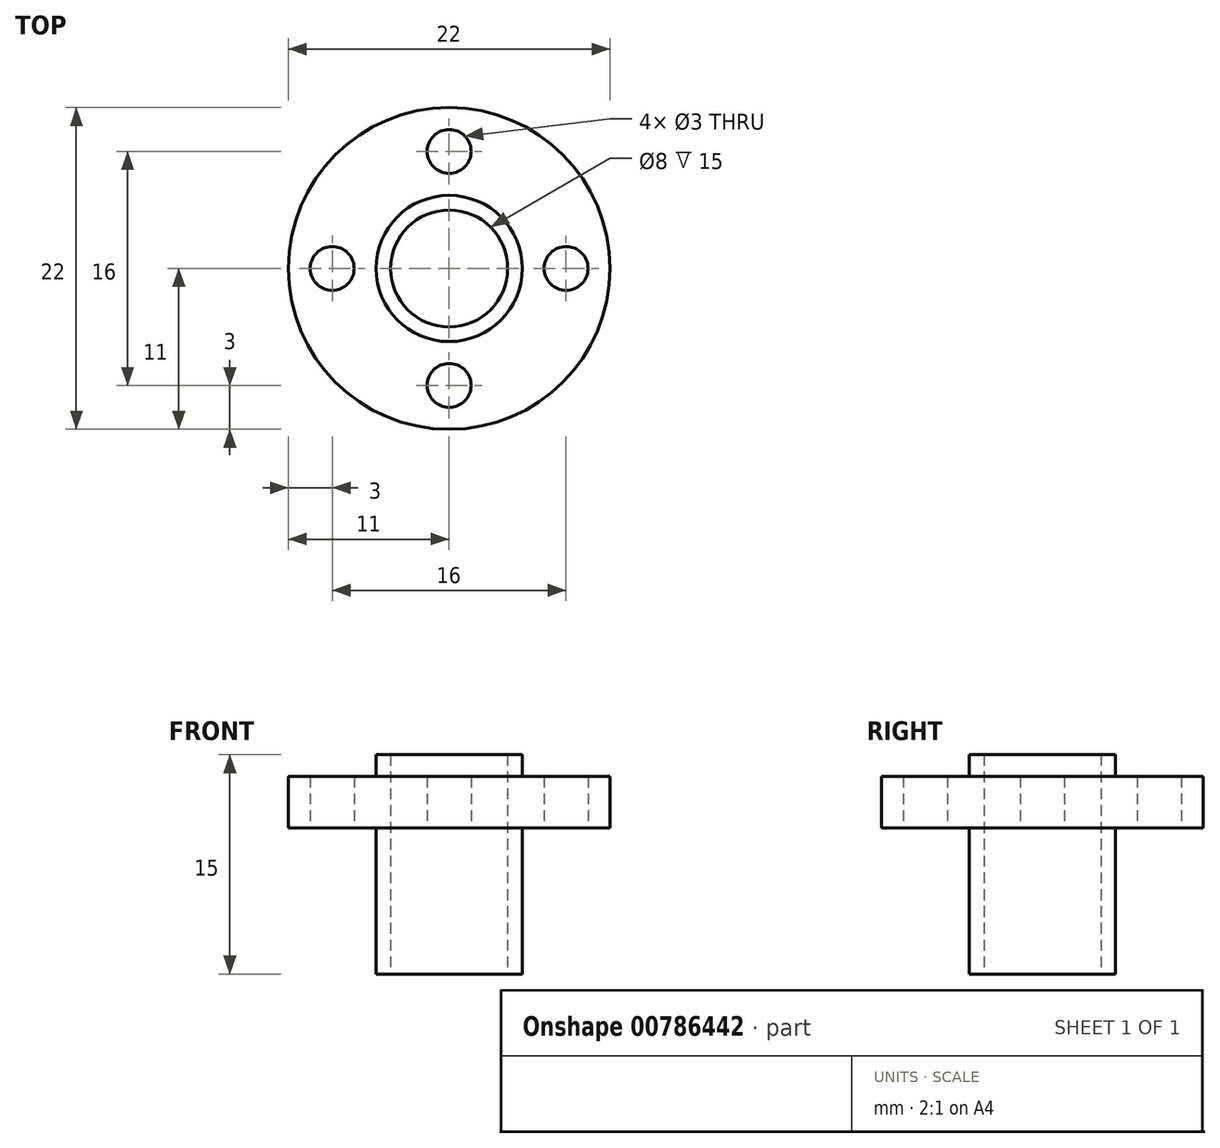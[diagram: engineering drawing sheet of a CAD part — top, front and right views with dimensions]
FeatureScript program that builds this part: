
annotation { "Feature Type Name" : "Feature", "Feature Type Description" : "" }
export const myFeature = defineFeature(function(context is Context, id is Id, definition is map)
    precondition{}
    {
        {
            var Q0;
            Q0=qCreatedBy(makeId("Top.planeOp"),FACE);
            var sketch = newSketch(context, id + "F0", { "sketchPlane" : qUnion([Q0])});
            skCircle(sketch, "E0", {"center": v(0, 0) * mm, "radius": 5 * mm});
            skCircle(sketch, "E1", {"center": v(0, 0) * mm, "radius": 4 * mm});
            skSolve(sketch);
        }
        {
            var Q0;
            Q0 = qSketchRegion(id + "F0", true);
            extrude(context, id + "F1", {"entities" : qUnion([Q0]), "depth" : 15 * mm, "offsetDistance" : 25 * mm});
        }
        {
            var Q0;
            Q0=qCreatedBy(makeId("Top.planeOp"),FACE);
            cPlane(context, id + "F2", {"entities" : qUnion([Q0]), "cplaneType" : CPlaneType.OFFSET, "offset" : 10 * mm, "width" : 150 * mm, "height" : 150 * mm});
        }
        {
            var Q0;
            Q0=qCreatedBy(id+"F2.planeOp",FACE);
            var sketch = newSketch(context, id + "F3", { "sketchPlane" : qUnion([Q0])});
            skCircle(sketch, "E2.0", {"center": v(0, 0) * mm, "radius": 4 * mm});
            skCircle(sketch, "E3", {"center": v(0, 0) * mm, "radius": 11 * mm});
            skCircle(sketch, "E4", {"center": v(0, 0) * mm, "radius": 8 * mm, "construction": true});
            skCircle(sketch, "E5", {"center": v(-8, 0) * mm, "radius": 1.5 * mm});
            skCircle(sketch, "E6", {"center": v(0, 8) * mm, "radius": 1.5 * mm});
            skCircle(sketch, "E7", {"center": v(0, -8) * mm, "radius": 1.5 * mm});
            skCircle(sketch, "E8", {"center": v(8, 0) * mm, "radius": 1.5 * mm});
            skLineSegment(sketch, "E9", {"start": v(0, 12.26) * mm, "end": v(0, -13.34) * mm, "construction": true});
            skLineSegment(sketch, "E10", {"start": v(-12.8, 0) * mm, "end": v(12.53, 0) * mm, "construction": true});
            skSolve(sketch);
        }
        {
            var Q0;
            Q0 = qSketchRegion(id + "F3", true);
            extrude(context, id + "F4", {"entities" : qUnion([Q0]), "operationType" : NewBodyOperationType.ADD, "depth" : 3.5 * mm, "offsetDistance" : 25 * mm});
        }
    });
